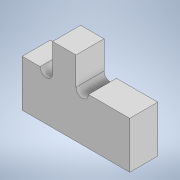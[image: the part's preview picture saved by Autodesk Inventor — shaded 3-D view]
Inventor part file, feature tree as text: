
AUTODESK INVENTOR PART (.ipt)
format: ipt  version: 2020 (Build 240168000, 168)  size: 111,616 bytes
history: native  units: mm
features: other x1, extrude x1
ambient origin geometry x8: Origin, YZ Plane, XZ Plane, XY Plane, X Axis, Y Axis, Z Axis, Center Point
bodies: Body1 (feature_tree)
feature tree (2):
  other  "CONTOURS"
  extrude  "Extrusion4"  Depth=18.0mm TaperAngle=0.0deg
